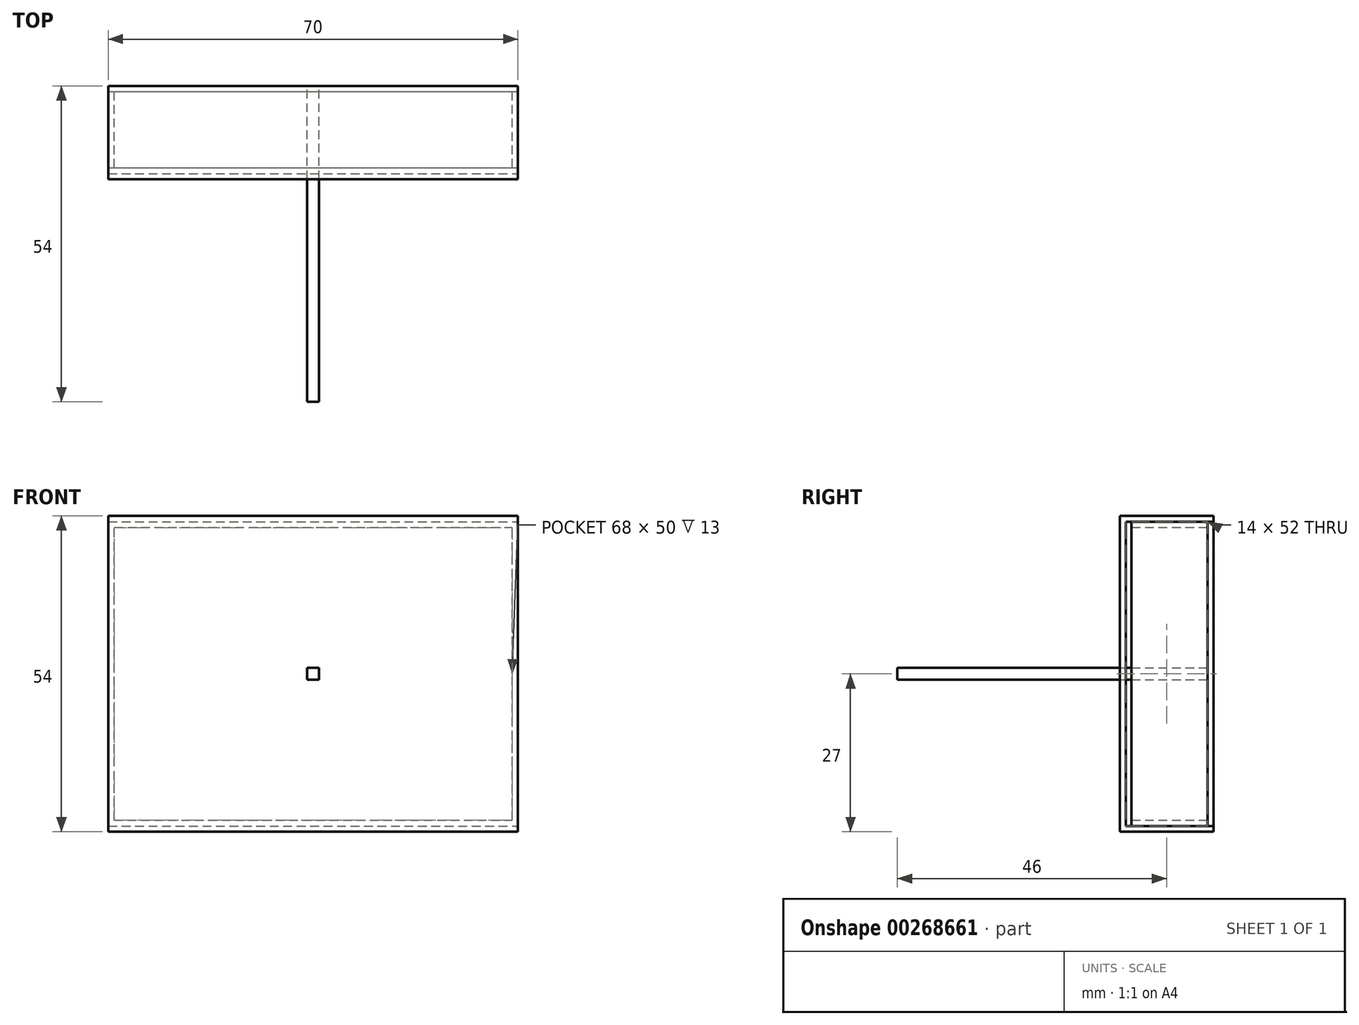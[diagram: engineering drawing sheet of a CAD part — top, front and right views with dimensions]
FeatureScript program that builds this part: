
annotation { "Feature Type Name" : "Feature", "Feature Type Description" : "" }
export const myFeature = defineFeature(function(context is Context, id is Id, definition is map)
    precondition{}
    {
        {
            var Q0;
            Q0=qCreatedBy(makeId("Front.planeOp"),FACE);
            var sketch = newSketch(context, id + "F0", { "sketchPlane" : qUnion([Q0])});
            skLineSegment(sketch, "E0.bottom", {"start": v(-35, -27) * mm, "end": v(35, -27) * mm});
            skLineSegment(sketch, "E0.top", {"start": v(-35, 27) * mm, "end": v(35, 27) * mm});
            skLineSegment(sketch, "E0.left", {"start": v(-35, -27) * mm, "end": v(-35, 27) * mm});
            skLineSegment(sketch, "E0.right", {"start": v(35, -27) * mm, "end": v(35, 27) * mm});
            skPoint(sketch, "E0.middle", {"position": v(0, 0) * mm});
            skSolve(sketch);
        }
        {
            var Q0;
            Q0 = qSketchRegion(id + "F0", true);
            extrude(context, id + "F1", {"entities" : qUnion([Q0]), "depth" : 16 * mm});
        }
        {
            var Q0;
            Q0=makeQuery(id+"F1.opExtrude","SWEPT_FACE",FACE,{"disambiguationData":[OSD([sQuery(id+"F0.wireOp",EDGE,"E0.right")])]});
            var Q1;
            Q1=makeQuery(id+"F1.opExtrude","SWEPT_FACE",FACE,{"disambiguationData":[OSD([sQuery(id+"F0.wireOp",EDGE,"E0.left")])]});
            shell(context, id + "F2", {"entities" : qUnion([Q0, Q1]), "thickness" : 1 * mm});
        }
        {
            var Q0;
            Q0=qCreatedBy(makeId("Front.planeOp"),FACE);
            var sketch = newSketch(context, id + "F3", { "sketchPlane" : qUnion([Q0])});
            skLineSegment(sketch, "E1.bottom", {"start": v(-35, -26) * mm, "end": v(35, -26) * mm});
            skLineSegment(sketch, "E1.top", {"start": v(-35, 26) * mm, "end": v(35, 26) * mm});
            skLineSegment(sketch, "E1.left", {"start": v(-35, -26) * mm, "end": v(-35, 26) * mm});
            skLineSegment(sketch, "E1.right", {"start": v(35, -26) * mm, "end": v(35, 26) * mm});
            skPoint(sketch, "E1.middle", {"position": v(0, 0) * mm});
            skSolve(sketch);
        }
        {
            var Q0;
            Q0=makeQuery(id+"F3.imprint","IMPRINT",FACE,{"disambiguationData":[TD([[makeQuery(id+"F3.imprint","IMPRINT",EDGE,{"derivedFrom":sQuery(id+"F3.wireOp",EDGE,"E1.bottom")}),1.0]])]});
            extrude(context, id + "F4", {"entities" : qUnion([Q0]), "depth" : 14 * mm});
        }
        {
            var Q0;
            Q0=makeQuery(id+"F4.opExtrude","CAP_FACE",FACE,{"disambiguationData":[OSD([sQuery(id+"F3.wireOp",EDGE,"E1.bottom"),sQuery(id+"F3.wireOp",EDGE,"E1.top"),sQuery(id+"F3.wireOp",EDGE,"E1.left"),sQuery(id+"F3.wireOp",EDGE,"E1.right")])],"isStart":false});
            shell(context, id + "F5", {"entities" : qUnion([Q0]), "thickness" : 1 * mm});
        }
        {
            var Q0;
            Q0=qCreatedBy(makeId("Front.planeOp"),FACE);
            var sketch = newSketch(context, id + "F6", { "sketchPlane" : qUnion([Q0])});
            skLineSegment(sketch, "E2.bottom", {"start": v(-1, -1) * mm, "end": v(1, -1) * mm});
            skLineSegment(sketch, "E2.top", {"start": v(-1, 1) * mm, "end": v(1, 1) * mm});
            skLineSegment(sketch, "E2.left", {"start": v(-1, -1) * mm, "end": v(-1, 1) * mm});
            skLineSegment(sketch, "E2.right", {"start": v(1, -1) * mm, "end": v(1, 1) * mm});
            skPoint(sketch, "E2.middle", {"position": v(0, 0) * mm});
            skSolve(sketch);
        }
        {
            var Q0;
            Q0=makeQuery(id+"F6.imprint","IMPRINT",FACE,{"disambiguationData":[TD([[makeQuery(id+"F6.imprint","IMPRINT",EDGE,{"derivedFrom":sQuery(id+"F6.wireOp",EDGE,"E2.bottom")}),1.0]])]});
            extrude(context, id + "F7", {"entities" : qUnion([Q0]), "depth" : 54 * mm});
        }
    });
